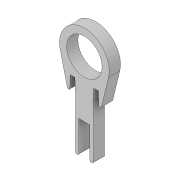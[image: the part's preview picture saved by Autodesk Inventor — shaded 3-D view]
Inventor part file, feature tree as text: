
AUTODESK INVENTOR PART (.ipt)
format: ipt  version: 2017 (Build 210142000, 142)  size: 163,840 bytes
history: native  units: in
note: dims shown in document units (in); Inventor stores cm internally (conversion verified against a paired STEP export)
features: sketch x3, other x2, chamfer x2, plane x2, sheet_metal_op x1, extrude x1, fillet x1, projected_geometry x1
ambient origin geometry x8: Origin, YZ Plane, XZ Plane, XY Plane, X Axis, Y Axis, Z Axis, Center Point
bodies: Solid1 (feature_tree)
feature tree (13):
  sheet_metal_op  "Face1"
  extrude  "Extrusion1"  Depth=0.3937in
  sketch  "Sketch3"  dims[d9=0.0623in d10=0.25in d11=0.25in d12=0.125in d14=0.125in d15=1.0in d16=0.0in d18=0.0573in d19=0.0573in d28=0.2362in d29=0.125in d30=0.2004in d31=0.1in d32=0.1in d33=0.0in d34=0.0179in d35=0.315in d36=0.0573in d37=0.015in d38=0.005in d39=0.125in d40=45.0deg d41=0.125in d42=0.005in d43=45.0deg]
  fillet  "Fillet4"  Radius=0.5512in
  other  "Work Axis1"
  chamfer  "Chamfer3"  Distance=0.25in
  chamfer  "Chamfer4"  Distance=0.25in
  sketch  "Sketch1"  dims[d2=0.1969in d3=0.3937in d4=0.5512in]
  other  "Plate1"
  sketch  "Sketch2"  dims[d8=0.0623in]
  projected_geometry  "Projected Loop1"
  plane  "Work Plane1"
  plane  "Work Plane2"
